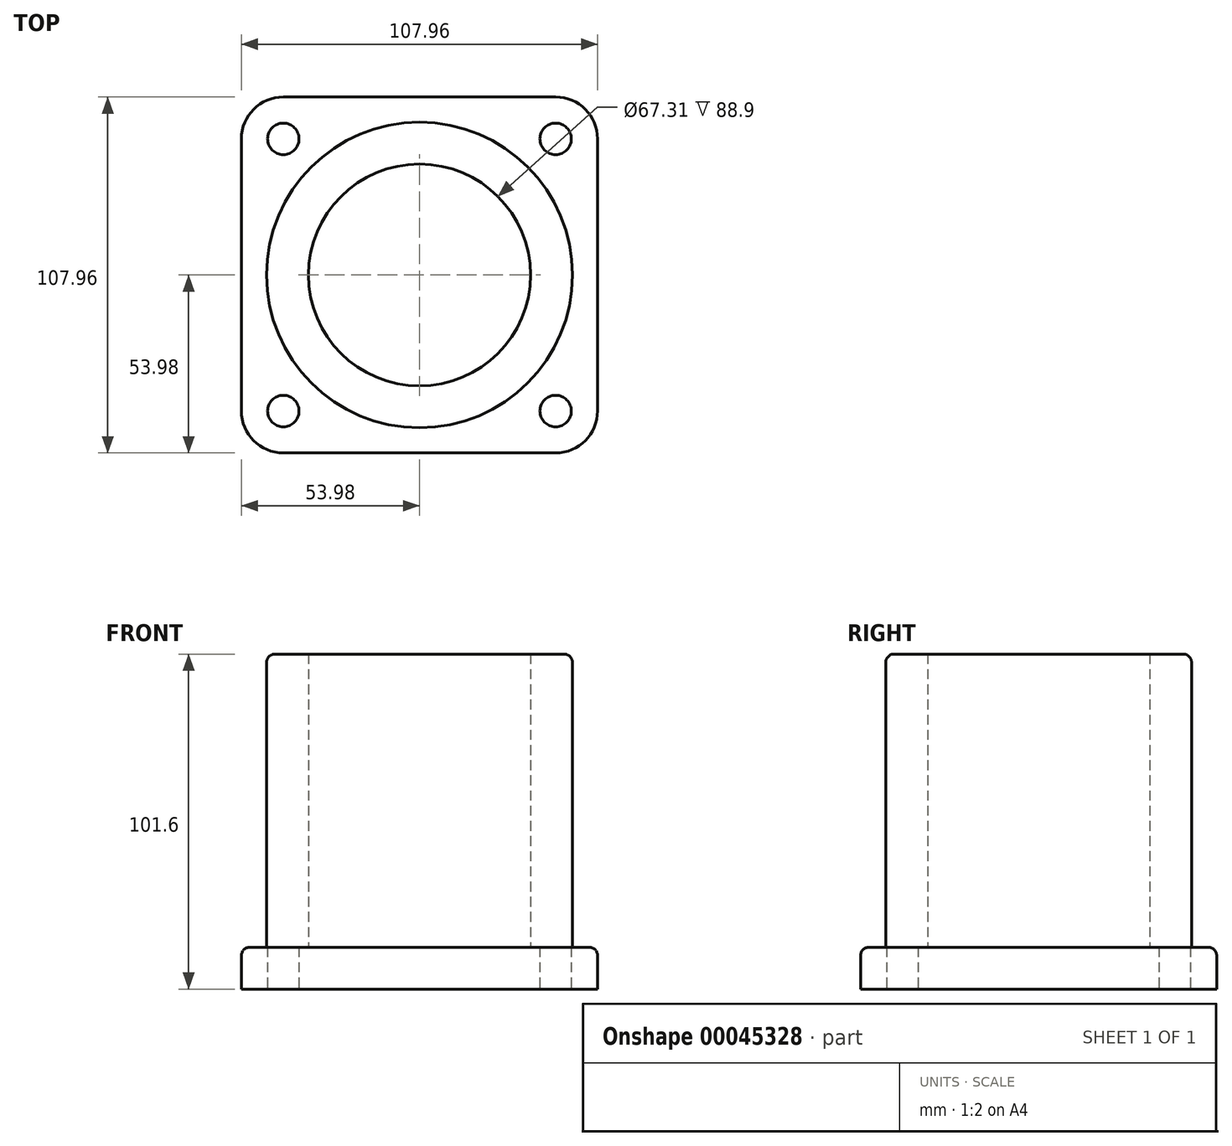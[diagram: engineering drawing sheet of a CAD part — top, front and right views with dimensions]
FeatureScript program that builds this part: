
annotation { "Feature Type Name" : "Feature", "Feature Type Description" : "" }
export const myFeature = defineFeature(function(context is Context, id is Id, definition is map)
    precondition{}
    {
        {
            var Q0;
            Q0=qCreatedBy(makeId("Top.planeOp"),FACE);
            var sketch = newSketch(context, id + "F0", { "sketchPlane" : qUnion([Q0])});
            skLineSegment(sketch, "E0.rect.bottom", {"start": v(41.27, 53.98) * mm, "end": v(-41.28, 53.98) * mm});
            skLineSegment(sketch, "E0.rect.top", {"start": v(41.27, -53.97) * mm, "end": v(-41.28, -53.97) * mm});
            skLineSegment(sketch, "E0.rect.left", {"start": v(53.98, 41.28) * mm, "end": v(53.98, -41.27) * mm});
            skLineSegment(sketch, "E0.rect.right", {"start": v(-53.98, 41.28) * mm, "end": v(-53.98, -41.27) * mm});
            skPoint(sketch, "E0.rect.middle", {"position": v(0, 0) * mm});
            skPoint(sketch, "E1.visualSharp", {"position": v(-53.98, 53.98) * mm});
            skArc(sketch, "E1.filletArc", {"start": v(-41.28, 53.98) * mm, "mid": v(-50.26, 50.26) * mm, "end": v(-53.98, 41.28) * mm});
            skPoint(sketch, "E2.visualSharp", {"position": v(53.98, 53.98) * mm});
            skArc(sketch, "E2.filletArc", {"start": v(53.98, 41.28) * mm, "mid": v(50.26, 50.26) * mm, "end": v(41.27, 53.98) * mm});
            skPoint(sketch, "E3.visualSharp", {"position": v(53.98, -53.97) * mm});
            skArc(sketch, "E3.filletArc", {"start": v(41.27, -53.97) * mm, "mid": v(50.26, -50.26) * mm, "end": v(53.98, -41.27) * mm});
            skPoint(sketch, "E4.visualSharp", {"position": v(-53.98, -53.97) * mm});
            skArc(sketch, "E4.filletArc", {"start": v(-53.98, -41.27) * mm, "mid": v(-50.26, -50.26) * mm, "end": v(-41.28, -53.97) * mm});
            skCircle(sketch, "E5", {"center": v(-41.28, 41.28) * mm, "radius": 4.76 * mm});
            skCircle(sketch, "E6", {"center": v(41.27, 41.27) * mm, "radius": 4.76 * mm});
            skCircle(sketch, "E7", {"center": v(41.27, -41.27) * mm, "radius": 4.76 * mm});
            skCircle(sketch, "E8", {"center": v(-41.28, -41.27) * mm, "radius": 4.76 * mm});
            skSolve(sketch);
        }
        {
            var Q0;
            Q0=makeQuery(id+"F0.imprint","IMPRINT",FACE,{"disambiguationData":[TD([[makeQuery(id+"F0.imprint","IMPRINT",EDGE,{"derivedFrom":sQuery(id+"F0.wireOp",EDGE,"E0.rect.bottom")}),1.0]])]});
            extrude(context, id + "F1", {"entities" : qUnion([Q0]), "depth" : 12.7 * mm});
        }
        {
            var Q0;
            Q0=makeQuery(id+"F1.opExtrude","CAP_FACE",FACE,{"disambiguationData":[OSD([sQuery(id+"F0.wireOp",EDGE,"E0.rect.bottom"),sQuery(id+"F0.wireOp",EDGE,"E0.rect.top"),sQuery(id+"F0.wireOp",EDGE,"E0.rect.left"),sQuery(id+"F0.wireOp",EDGE,"E0.rect.right"),sQuery(id+"F0.wireOp",EDGE,"E1.filletArc"),sQuery(id+"F0.wireOp",EDGE,"E2.filletArc"),sQuery(id+"F0.wireOp",EDGE,"E3.filletArc"),sQuery(id+"F0.wireOp",EDGE,"E4.filletArc"),sQuery(id+"F0.wireOp",EDGE,"E5"),sQuery(id+"F0.wireOp",EDGE,"E6"),sQuery(id+"F0.wireOp",EDGE,"E7"),sQuery(id+"F0.wireOp",EDGE,"E8")])],"isStart":false});
            var sketch = newSketch(context, id + "F2", { "sketchPlane" : qUnion([Q0])});
            skCircle(sketch, "E9", {"center": v(0, 0) * mm, "radius": 33.66 * mm});
            skCircle(sketch, "E10", {"center": v(0, 0) * mm, "radius": 46.35 * mm});
            skSolve(sketch);
        }
        {
            var Q0;
            Q0=makeQuery(id+"F2.imprint","IMPRINT",FACE,{"disambiguationData":[TD([[makeQuery(id+"F2.imprint","IMPRINT",EDGE,{"derivedFrom":sQuery(id+"F2.wireOp",EDGE,"E9")}),-1.0]])]});
            extrude(context, id + "F3", {"entities" : qUnion([Q0]), "operationType" : NewBodyOperationType.ADD, "depth" : 88.9 * mm});
        }
        {
            var Q0;
            Q0=makeQuery(id+"F3.opExtrude","CAP_EDGE",EDGE,{"disambiguationData":[OSD([sQuery(id+"F2.wireOp",EDGE,"E10")])],"isStart":true});
            var Q1;
            Q1=makeQuery(id+"F1.opExtrude","CAP_EDGE",EDGE,{"disambiguationData":[OSD([sQuery(id+"F0.wireOp",EDGE,"E0.rect.top")])],"isStart":false});
            var Q2;
            Q2=makeQuery(id+"F3.opExtrude","CAP_EDGE",EDGE,{"disambiguationData":[OSD([sQuery(id+"F2.wireOp",EDGE,"E10")])],"isStart":false});
            fillet(context, id + "F4", {"entities" : qUnion([Q0, Q1, Q2]), "radius" : 2.54 * mm, "tangentPropagation" : true, "allowEdgeOverflow" : false});
        }
    });
